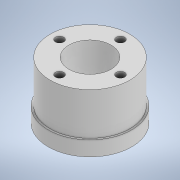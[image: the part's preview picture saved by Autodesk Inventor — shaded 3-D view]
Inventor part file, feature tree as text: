
AUTODESK INVENTOR PART (.ipt)
format: ipt  version: 2022.2 (Build 262287010, 287A)  size: 128,000 bytes
history: native  units: in
note: dims shown in document units (in); Inventor stores cm internally (conversion verified against a paired STEP export)
features: extrude x4, sketch x4, other x1
ambient origin geometry x8: Origin, YZ Plane, XZ Plane, XY Plane, X Axis, Y Axis, Z Axis, Center Point
bodies: Body1 (feature_tree)
feature tree (9):
  other  "Sólido1"
  extrude  "Extrusión1"  Depth=0.1378in TaperAngle=0.0deg
  extrude  "Extrusión2"  Depth=0.3937in TaperAngle=0.0deg
  extrude  "Extrusión3"  TaperAngle=0.0deg  [1 undecoded]
  extrude  "Extrusión4"  Depth=0.3937in
  sketch  "Boceto1"  dims[d0=0.7795in d1=0.1378in d2=0.0in]
  sketch  "Boceto2"  dims[d3=0.7441in d4=0.3937in d5=0.0in]
  sketch  "Boceto3"  dims[d6=0.3937in d7=0.0in d8=0.0in]
  sketch  "Boceto4"  dims[d9=0.0787in d10=0.0787in d11=0.3937in d12=0.0in]
note: 1 required parameter value undecoded (feature->parameter linkage not recoverable at this tier; creation-order binding heuristic only, values carry confidence <= 0.55)
